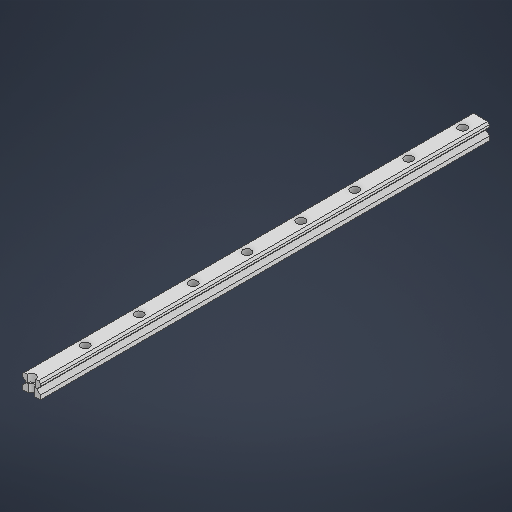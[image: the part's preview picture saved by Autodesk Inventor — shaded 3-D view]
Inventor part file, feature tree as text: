
AUTODESK INVENTOR PART (.ipt)
format: ipt  version: 2025.1 (Build 291241000, 241)  size: 243,200 bytes
history: native  units: mm
features: extrude x3, sketch x2, pattern_linear x1
ambient origin geometry x8: Origin, YZ Plane, XZ Plane, XY Plane, X Axis, Y Axis, Z Axis, Center Point
bodies: Solid1 (feature_tree)
feature tree (6):
  extrude  "Extrusion1"  Depth=20.0mm
  sketch  "Sketch2"  dims[d2=4.6mm d3=8.5mm d8=135.0deg d9=0.5mm d10=135.0deg d11=2.5mm d12=500.0mm d13=0.0mm d14=20.0mm d15=60.0mm d16=9.5mm d17=6.0mm d18=8.5mm d19=0.0mm d20=8.5mm d21=0.0mm d22=90.0mm d24=60.0mm]
  extrude  "Extrusion2"  Depth=8.5mm
  extrude  "Extrusion3"  TaperAngle=135.0deg  [1 undecoded]
  pattern_linear  "Rectangular Pattern1"  Spacing1=0.5mm  [1 undecoded]
  sketch  "Sketch1"  dims[d0=17.5mm d1=20.0mm]
note: 2 required parameter values undecoded (feature->parameter linkage not recoverable at this tier; creation-order binding heuristic only, values carry confidence <= 0.55)
